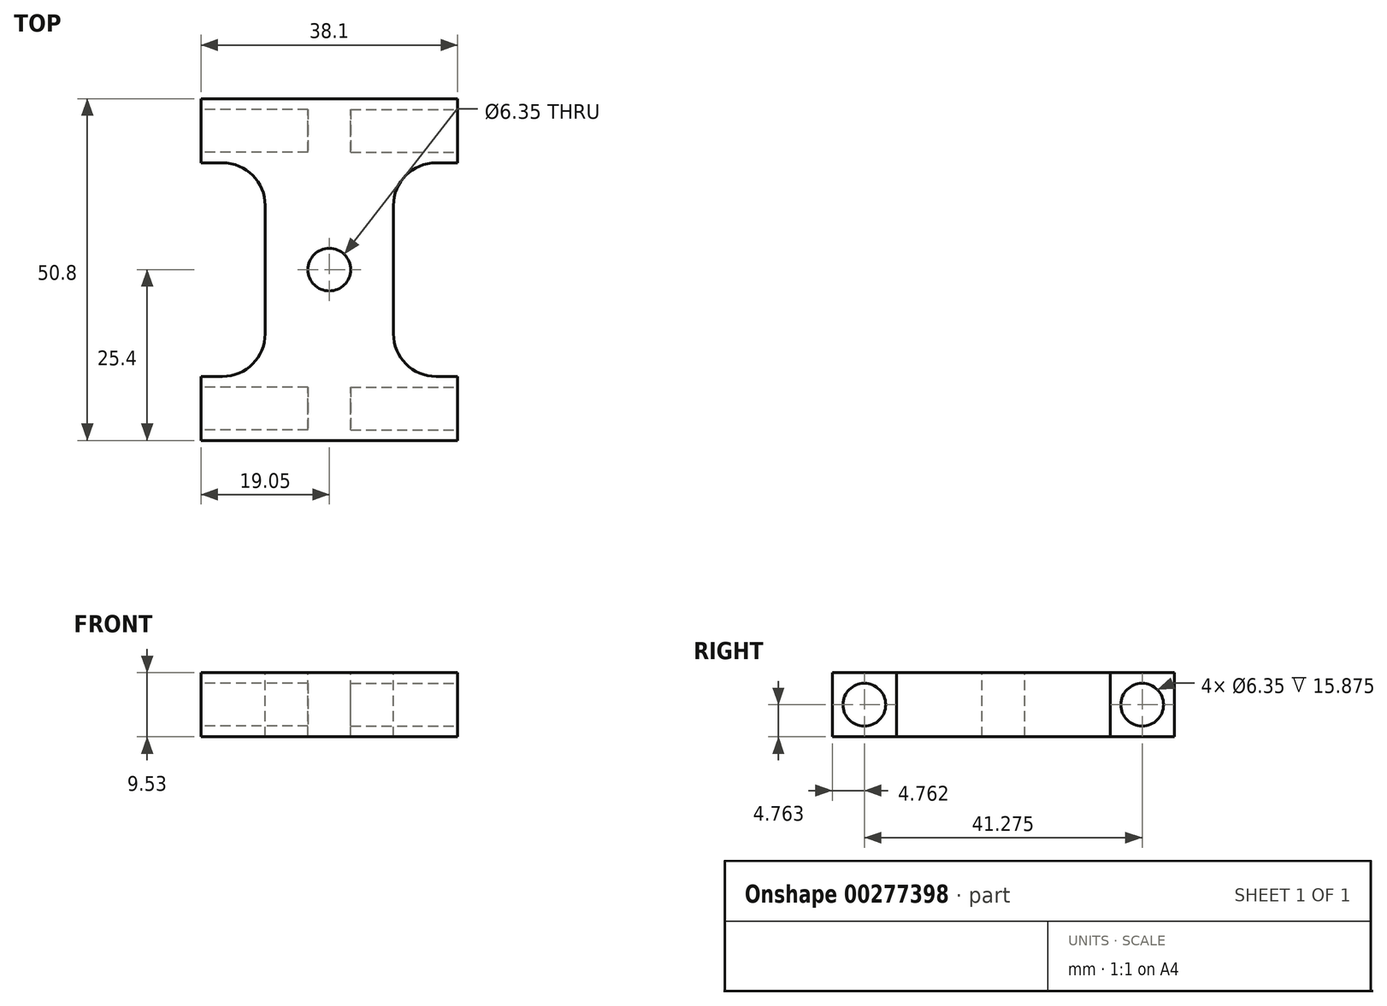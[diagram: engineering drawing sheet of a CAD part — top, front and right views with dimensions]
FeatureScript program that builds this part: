
annotation { "Feature Type Name" : "Feature", "Feature Type Description" : "" }
export const myFeature = defineFeature(function(context is Context, id is Id, definition is map)
    precondition{}
    {
        {
            var Q0;
            Q0=qCreatedBy(makeId("Top.planeOp"),FACE);
            var sketch = newSketch(context, id + "F0", { "sketchPlane" : qUnion([Q0])});
            skLineSegment(sketch, "E0.bottom", {"start": v(19.05, 25.4) * mm, "end": v(-19.05, 25.4) * mm});
            skLineSegment(sketch, "E0.top", {"start": v(19.05, -25.4) * mm, "end": v(-19.05, -25.4) * mm});
            skLineSegment(sketch, "E0.left", {"start": v(19.05, 25.4) * mm, "end": v(19.05, -25.4) * mm});
            skLineSegment(sketch, "E0.right", {"start": v(-19.05, 25.4) * mm, "end": v(-19.05, -25.4) * mm});
            skPoint(sketch, "E0.middle", {"position": v(0, 0) * mm});
            skSolve(sketch);
        }
        {
            var Q0;
            Q0 = qSketchRegion(id + "F0", true);
            extrude(context, id + "F1", {"entities" : qUnion([Q0]), "depth" : 9.52 * mm});
        }
        {
            var Q0;
            Q0=makeQuery(id+"F1.opExtrude","CAP_FACE",FACE,{"disambiguationData":[OSD([sQuery(id+"F0.wireOp",EDGE,"E0.bottom"),sQuery(id+"F0.wireOp",EDGE,"E0.top"),sQuery(id+"F0.wireOp",EDGE,"E0.left"),sQuery(id+"F0.wireOp",EDGE,"E0.right")])],"isStart":false});
            var sketch = newSketch(context, id + "F2", { "sketchPlane" : qUnion([Q0])});
            skLineSegment(sketch, "E1.bottom", {"start": v(-19.05, 15.88) * mm, "end": v(-15.88, 15.88) * mm});
            skLineSegment(sketch, "E1.top", {"start": v(-19.05, -15.88) * mm, "end": v(-15.88, -15.88) * mm});
            skLineSegment(sketch, "E1.left", {"start": v(-19.05, 15.88) * mm, "end": v(-19.05, -15.88) * mm});
            skLineSegment(sketch, "E1.right", {"start": v(-9.53, 9.53) * mm, "end": v(-9.53, -9.52) * mm});
            skLineSegment(sketch, "E2.bottom", {"start": v(15.88, 15.88) * mm, "end": v(19.05, 15.88) * mm});
            skLineSegment(sketch, "E2.top", {"start": v(15.88, -15.87) * mm, "end": v(19.05, -15.87) * mm});
            skLineSegment(sketch, "E2.left", {"start": v(9.53, 9.53) * mm, "end": v(9.53, -9.52) * mm});
            skLineSegment(sketch, "E2.right", {"start": v(19.05, 15.88) * mm, "end": v(19.05, -15.87) * mm});
            skPoint(sketch, "E3.visualSharp", {"position": v(-9.53, 15.88) * mm});
            skArc(sketch, "E3.filletArc", {"start": v(-9.53, 9.53) * mm, "mid": v(-11.38, 14.02) * mm, "end": v(-15.88, 15.88) * mm});
            skPoint(sketch, "E4.visualSharp", {"position": v(-9.53, -15.88) * mm});
            skArc(sketch, "E4.filletArc", {"start": v(-15.88, -15.88) * mm, "mid": v(-11.38, -14.02) * mm, "end": v(-9.52, -9.52) * mm});
            skPoint(sketch, "E5.visualSharp", {"position": v(9.53, 15.88) * mm});
            skArc(sketch, "E5.filletArc", {"start": v(15.88, 15.88) * mm, "mid": v(11.38, 14.02) * mm, "end": v(9.53, 9.53) * mm});
            skPoint(sketch, "E6.visualSharp", {"position": v(9.53, -15.87) * mm});
            skArc(sketch, "E6.filletArc", {"start": v(9.53, -9.52) * mm, "mid": v(11.38, -14.02) * mm, "end": v(15.88, -15.87) * mm});
            skSolve(sketch);
        }
        {
            var Q0;
            Q0 = qSketchRegion(id + "F2", true);
            extrude(context, id + "F3", {"entities" : qUnion([Q0]), "operationType" : NewBodyOperationType.REMOVE, "endBound" : BoundingType.THROUGH_ALL, "oppositeDirection" : true, "depth" : 25.4 * mm});
        }
        {
            var Q0;
            {var subQ1=sQuery(id+"F0.wireOp",EDGE,"E0.left");var subQ2=sQuery(id+"F0.wireOp",EDGE,"E0.top");Q0=makeQuery(id+"F3.boolean.opBoolean","SPLIT",FACE,{"disambiguationData":[TD([makeQuery(id+"F1.opExtrude","SWEPT_FACE",FACE,{"disambiguationData":[OSD([subQ2])]})])],"derivedFrom":makeQuery(id+"F1.opExtrude","SWEPT_FACE",FACE,{"disambiguationData":[OSD([subQ1])]})});}
            var sketch = newSketch(context, id + "F4", { "sketchPlane" : qUnion([Q0])});
            skCircle(sketch, "E7", {"center": v(-20.64, 4.76) * mm, "radius": 3.18 * mm});
            skPoint(sketch, "E7.centerSnap0", {"position": v(-20.64, 9.53) * mm});
            skPoint(sketch, "E7.centerSnap1", {"position": v(-15.88, 4.76) * mm});
            skCircle(sketch, "E8", {"center": v(20.64, 4.76) * mm, "radius": 3.18 * mm});
            skSolve(sketch);
        }
        {
            var Q0;
            Q0 = qSketchRegion(id + "F4", true);
            extrude(context, id + "F5", {"entities" : qUnion([Q0]), "operationType" : NewBodyOperationType.REMOVE, "oppositeDirection" : true, "depth" : 15.88 * mm, "offsetDistance" : 25.4 * mm});
        }
        {
            var Q0;
            Q0=makeQuery(id+"F1.opExtrude","CAP_FACE",FACE,{"disambiguationData":[OSD([sQuery(id+"F0.wireOp",EDGE,"E0.bottom"),sQuery(id+"F0.wireOp",EDGE,"E0.top"),sQuery(id+"F0.wireOp",EDGE,"E0.left"),sQuery(id+"F0.wireOp",EDGE,"E0.right")])],"isStart":false});
            var sketch = newSketch(context, id + "F6", { "sketchPlane" : qUnion([Q0])});
            skCircle(sketch, "E9", {"center": v(0, 0) * mm, "radius": 3.18 * mm});
            skSolve(sketch);
        }
        {
            var Q0;
            Q0 = qSketchRegion(id + "F6", true);
            extrude(context, id + "F7", {"entities" : qUnion([Q0]), "operationType" : NewBodyOperationType.REMOVE, "endBound" : BoundingType.THROUGH_ALL, "oppositeDirection" : true, "depth" : 25.4 * mm, "offsetDistance" : 25.4 * mm});
        }
        {
            var Q0;
            {var subQ0=sQuery(id+"F0.wireOp",EDGE,"E0.bottom");var subQ1=sQuery(id+"F0.wireOp",EDGE,"E0.right");Q0=makeQuery(id+"F3.boolean.opBoolean","SPLIT",FACE,{"disambiguationData":[TD([makeQuery(id+"F1.opExtrude","SWEPT_FACE",FACE,{"disambiguationData":[OSD([subQ0])]})])],"derivedFrom":makeQuery(id+"F1.opExtrude","SWEPT_FACE",FACE,{"disambiguationData":[OSD([subQ1])]})});}
            var sketch = newSketch(context, id + "F8", { "sketchPlane" : qUnion([Q0])});
            skCircle(sketch, "E10", {"center": v(-20.64, 4.76) * mm, "radius": 3.18 * mm});
            skPoint(sketch, "E10.centerSnap0", {"position": v(-15.88, 4.76) * mm});
            skPoint(sketch, "E10.centerSnap1", {"position": v(-20.64, 9.53) * mm});
            skCircle(sketch, "E11.MirrorC", {"center": v(20.64, 4.76) * mm, "radius": 3.18 * mm});
            skSolve(sketch);
        }
        {
            var Q0;
            Q0 = qSketchRegion(id + "F8", true);
            extrude(context, id + "F9", {"entities" : qUnion([Q0]), "operationType" : NewBodyOperationType.REMOVE, "oppositeDirection" : true, "depth" : 15.88 * mm, "offsetDistance" : 25.4 * mm});
        }
    });
